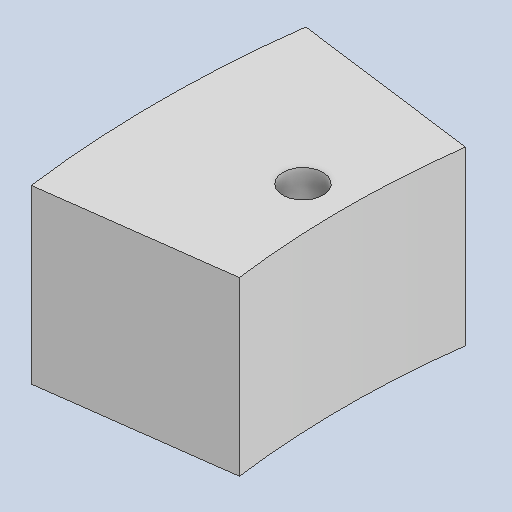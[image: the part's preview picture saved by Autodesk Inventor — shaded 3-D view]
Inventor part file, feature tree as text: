
AUTODESK INVENTOR PART (.ipt)
format: ipt  version: 2025.1 (Build 291241020, 241B)  size: 100,352 bytes
history: native  units: in
note: dims shown in document units (in); Inventor stores cm internally (conversion verified against a paired STEP export)
features: extrude x1, sketch x1
ambient origin geometry x8: Origin, YZ Plane, XZ Plane, XY Plane, X Axis, Y Axis, Z Axis, Center Point
bodies: Solid1 (feature_tree)
feature tree (2):
  extrude  "Extrusion1"  Depth=0.9in
  sketch  "Sketch1"  dims[d0=0.209in d1=1.0in d2=0.9in d3=0.0in d4=9.5in d5=10.0in d6=7.25in d7=0.0515in d8=0.0515in d9=0.22in d10=11.0in]
